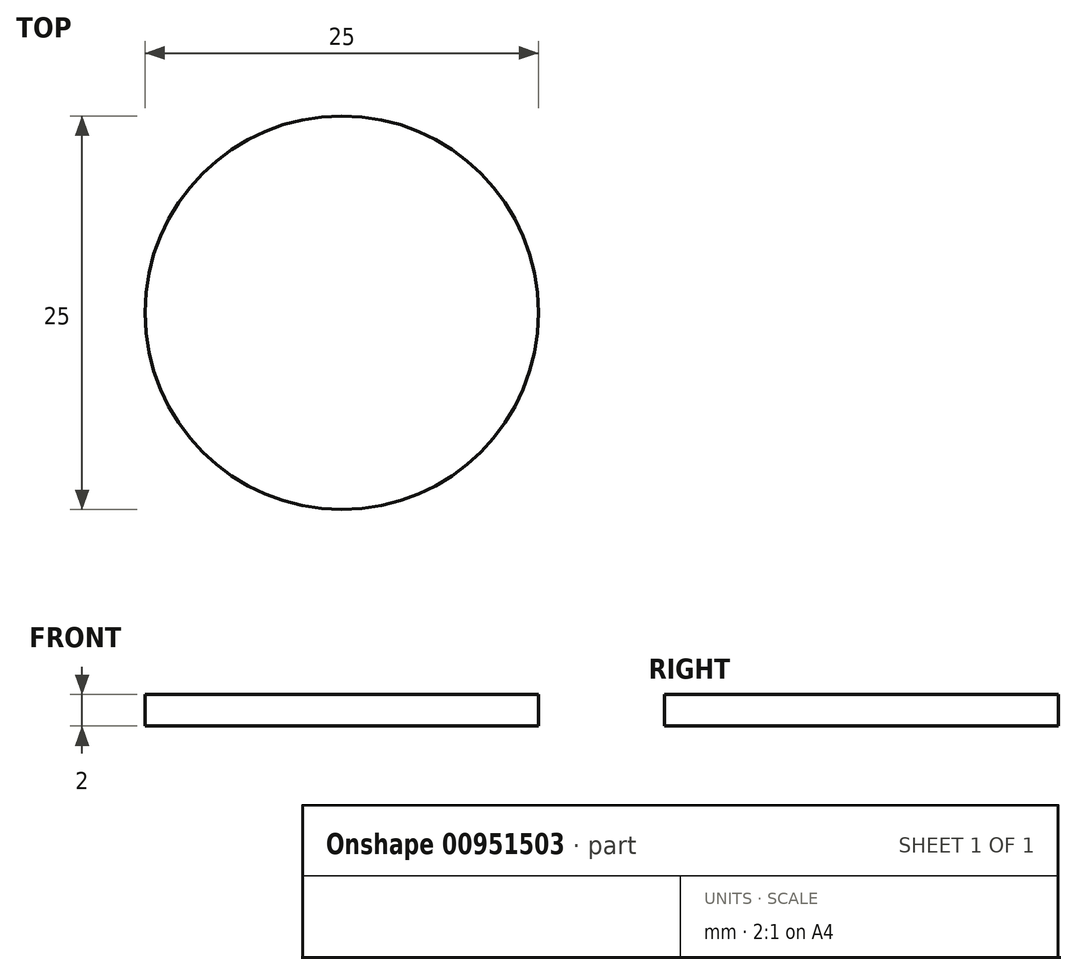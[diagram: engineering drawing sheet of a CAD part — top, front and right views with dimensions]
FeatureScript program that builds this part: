
annotation { "Feature Type Name" : "Feature", "Feature Type Description" : "" }
export const myFeature = defineFeature(function(context is Context, id is Id, definition is map)
    precondition{}
    {
        {
            var Q0;
            Q0=qCreatedBy(makeId("Top.planeOp"),FACE);
            var sketch = newSketch(context, id + "F0", { "sketchPlane" : qUnion([Q0])});
            skCircle(sketch, "E0", {"center": v(0, 0) * mm, "radius": 12.5 * mm});
            skSolve(sketch);
        }
        {
            var Q0;
            Q0=makeQuery(id+"F0.imprint","IMPRINT",FACE,{"disambiguationData":[TD([[makeQuery(id+"F0.imprint","IMPRINT",EDGE,{"derivedFrom":sQuery(id+"F0.wireOp",EDGE,"E0")}),1.0]])]});
            extrude(context, id + "F1", {"entities" : qUnion([Q0]), "depth" : 2 * mm, "offsetDistance" : 25 * mm});
        }
    });
